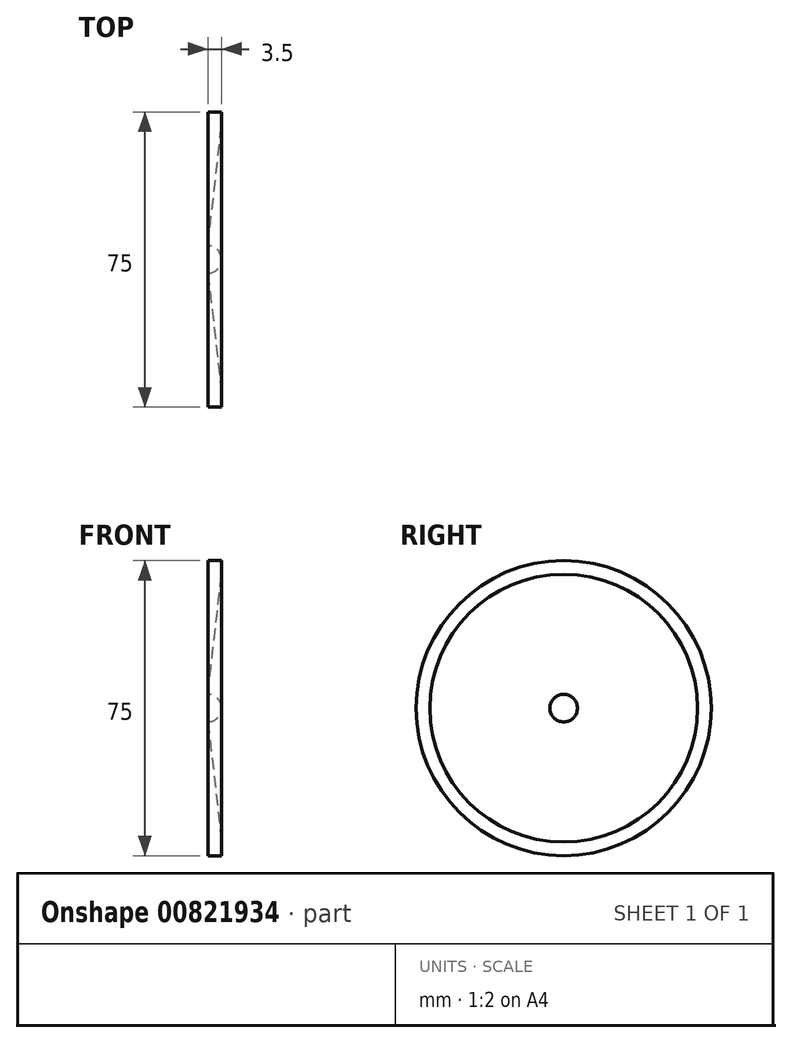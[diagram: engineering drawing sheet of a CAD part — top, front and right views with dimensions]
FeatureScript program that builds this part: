
annotation { "Feature Type Name" : "Feature", "Feature Type Description" : "" }
export const myFeature = defineFeature(function(context is Context, id is Id, definition is map)
    precondition{}
    {
        {
            var Q0;
            Q0=qCreatedBy(makeId("Front.planeOp"),FACE);
            var sketch = newSketch(context, id + "F0", { "sketchPlane" : qUnion([Q0])});
            skLineSegment(sketch, "E0", {"start": v(0, 0) * mm, "end": v(0, 37.5) * mm});
            skLineSegment(sketch, "E1", {"start": v(0, 37.5) * mm, "end": v(3.5, 37.5) * mm});
            skArc(sketch, "E2", {"start": v(0, 3.5) * mm, "mid": v(2.47, 2.47) * mm, "end": v(3.5, 0) * mm});
            skLineSegment(sketch, "E3", {"start": v(0, 0) * mm, "end": v(3.5, 0) * mm});
            skLineSegment(sketch, "E4", {"start": v(3.5, 37.5) * mm, "end": v(3.5, 34) * mm});
            skLineSegment(sketch, "E5", {"start": v(0, 3.5) * mm, "end": v(3.5, 34) * mm});
            skSolve(sketch);
        }
        {
            var Q0;
            Q0=qSketchRegion(id+"F0",true);
            var Q1;
            Q1=sQuery(id+"F0.wireOp",EDGE,"E3");
            revolve(context, id + "F1", {"surfaceOperationType" : NewSurfaceOperationType.NEW, "entities" : qUnion([Q0]), "axis" : qUnion([Q1]), "revolveType" : RevolveType.FULL});
        }
    });
